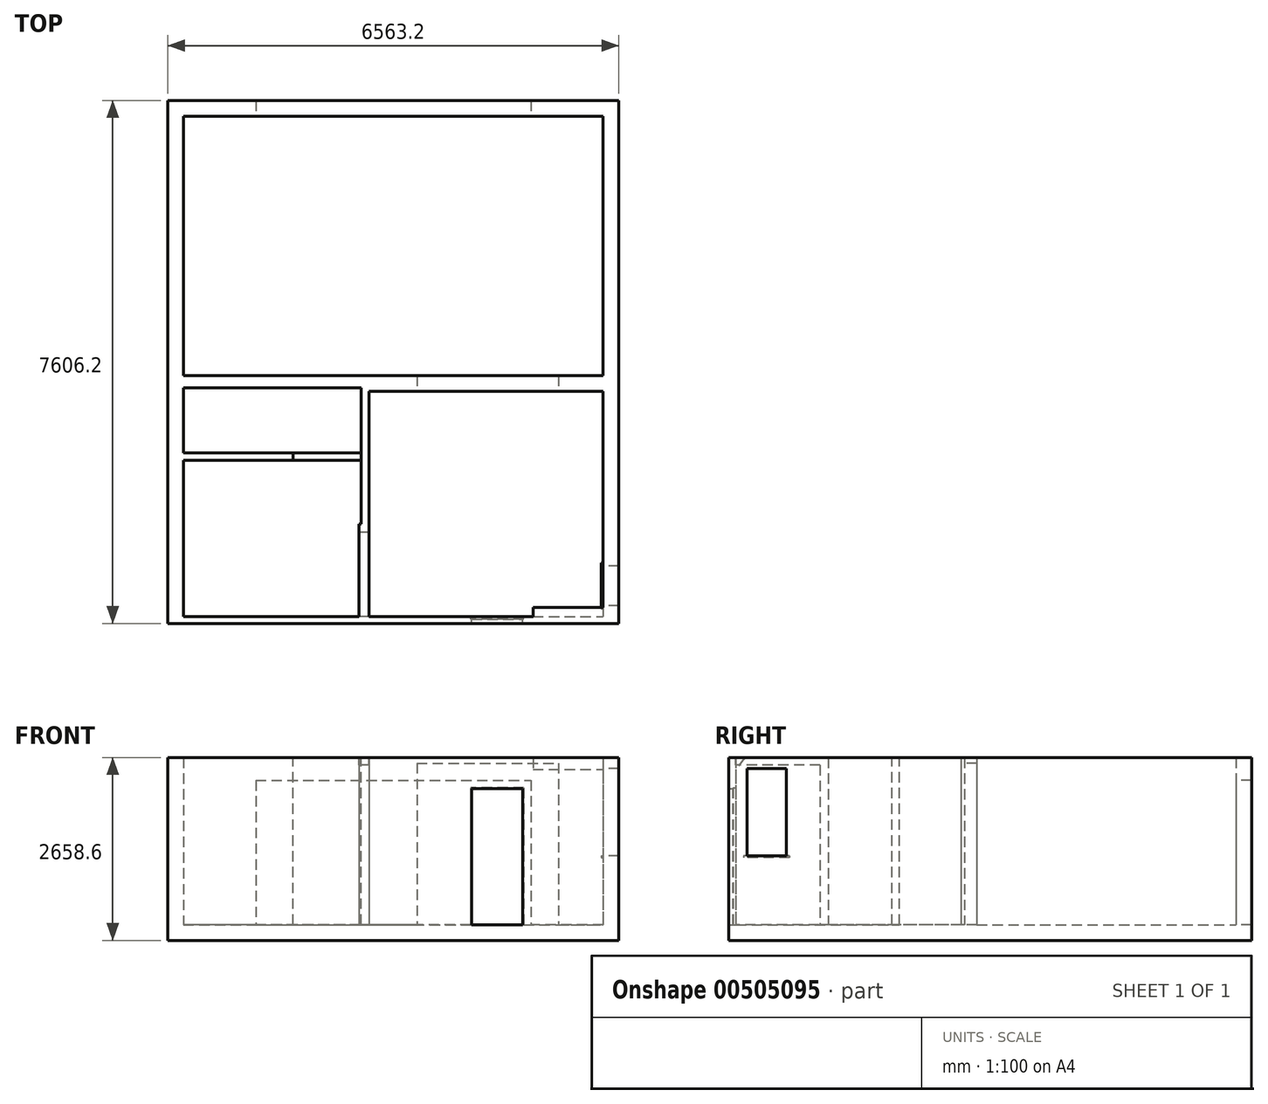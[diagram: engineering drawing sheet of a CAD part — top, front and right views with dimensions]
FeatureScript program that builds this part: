
annotation { "Feature Type Name" : "Feature", "Feature Type Description" : "" }
export const myFeature = defineFeature(function(context is Context, id is Id, definition is map)
    precondition{}
    {
        {
            var Q0;
            Q0=qCreatedBy(makeId("Top.planeOp"),FACE);
            var sketch = newSketch(context, id + "F0", { "sketchPlane" : qUnion([Q0])});
            skLineSegment(sketch, "E0", {"start": v(-3026.66, 951.57) * mm, "end": v(369.34, 951.57) * mm});
            skLineSegment(sketch, "E1", {"start": v(369.34, 951.57) * mm, "end": v(369.34, 722.97) * mm});
            skLineSegment(sketch, "E2", {"start": v(369.34, 722.97) * mm, "end": v(-327.66, 722.97) * mm});
            skLineSegment(sketch, "E3", {"start": v(-327.66, 722.97) * mm, "end": v(-327.66, -1327.03) * mm});
            skLineSegment(sketch, "E4", {"start": v(-327.66, -1327.03) * mm, "end": v(-1537.66, -1327.03) * mm});
            skLineSegment(sketch, "E5", {"start": v(-3255.26, 951.57) * mm, "end": v(-3255.26, -2250.1) * mm});
            skLineSegment(sketch, "E6", {"start": v(2429.34, 951.57) * mm, "end": v(3079.34, 951.57) * mm});
            skLineSegment(sketch, "E7", {"start": v(2429.34, 951.57) * mm, "end": v(2429.34, 722.97) * mm});
            skLineSegment(sketch, "E8", {"start": v(3307.94, 951.57) * mm, "end": v(3307.94, -2660.36) * mm});
            skLineSegment(sketch, "E9", {"start": v(2429.34, 722.97) * mm, "end": v(3079.34, 722.97) * mm});
            skLineSegment(sketch, "E10", {"start": v(3079.34, 722.97) * mm, "end": v(3079.34, -2553.03) * mm});
            skLineSegment(sketch, "E11", {"start": v(3079.34, 951.57) * mm, "end": v(3079.34, 4722.97) * mm});
            skLineSegment(sketch, "E12", {"start": v(3079.34, 4722.97) * mm, "end": v(-3026.66, 4722.97) * mm});
            skLineSegment(sketch, "E13", {"start": v(-3026.66, 4722.97) * mm, "end": v(-3026.66, 951.57) * mm});
            skLineSegment(sketch, "E14", {"start": v(-3255.26, 951.57) * mm, "end": v(-3255.26, 4951.57) * mm});
            skLineSegment(sketch, "E15", {"start": v(-3255.26, 4951.57) * mm, "end": v(3307.94, 4951.57) * mm});
            skLineSegment(sketch, "E16", {"start": v(3307.94, 4951.57) * mm, "end": v(3307.94, 951.57) * mm});
            skLineSegment(sketch, "E17", {"start": v(-1537.66, -2553.03) * mm, "end": v(3079.34, -2553.03) * mm});
            skLineSegment(sketch, "E18", {"start": v(-3255.26, -2654.63) * mm, "end": v(3307.94, -2654.63) * mm});
            skLineSegment(sketch, "E19", {"start": v(-1537.66, -2553.03) * mm, "end": v(-1537.66, -1327.03) * mm});
            skLineSegment(sketch, "E20", {"start": v(-1670.66, -1327.03) * mm, "end": v(-1670.66, -2553.03) * mm});
            skLineSegment(sketch, "E21", {"start": v(-1670.66, -2553.03) * mm, "end": v(-3026.66, -2553.03) * mm});
            skLineSegment(sketch, "E22", {"start": v(-3026.66, -2553.03) * mm, "end": v(-3026.66, -1327.03) * mm});
            skLineSegment(sketch, "E23", {"start": v(-3026.66, -1327.03) * mm, "end": v(-1670.66, -1327.03) * mm});
            skLineSegment(sketch, "E24", {"start": v(-3255.26, -2250.1) * mm, "end": v(-3255.26, -2654.63) * mm});
            skLineSegment(sketch, "E25", {"start": v(-2642.66, 772.97) * mm, "end": v(-1542.66, 772.97) * mm});
            skLineSegment(sketch, "E26", {"start": v(-442.66, 772.97) * mm, "end": v(-442.66, -1207.03) * mm});
            skLineSegment(sketch, "E27", {"start": v(-442.66, -1207.03) * mm, "end": v(-1432.66, -1207.03) * mm});
            skLineSegment(sketch, "E28", {"start": v(-1432.66, -1207.03) * mm, "end": v(-1432.66, 772.97) * mm});
            skLineSegment(sketch, "E29", {"start": v(-3026.66, -960.06) * mm, "end": v(-3026.66, -282.03) * mm});
            skLineSegment(sketch, "E30", {"start": v(-2642.66, 772.97) * mm, "end": v(-3026.66, 772.97) * mm});
            skLineSegment(sketch, "E31", {"start": v(-1542.66, 772.97) * mm, "end": v(-1542.66, -172.03) * mm});
            skLineSegment(sketch, "E32", {"start": v(-1542.66, -1212.03) * mm, "end": v(-3026.66, -1212.03) * mm});
            skLineSegment(sketch, "E33", {"start": v(-3026.66, -960.06) * mm, "end": v(-3026.66, -1212.03) * mm});
            skLineSegment(sketch, "E34", {"start": v(-3026.66, -172.03) * mm, "end": v(-3026.66, -172.03) * mm});
            skLineSegment(sketch, "E35", {"start": v(-3026.66, -282.03) * mm, "end": v(-1542.66, -282.03) * mm});
            skLineSegment(sketch, "E36", {"start": v(-3026.66, 0) * mm, "end": v(-3026.66, 772.97) * mm});
            skLineSegment(sketch, "E37", {"start": v(-3026.66, -172.03) * mm, "end": v(-1542.66, -172.03) * mm});
            skLineSegment(sketch, "E38", {"start": v(-3026.66, 0) * mm, "end": v(-3026.66, -172.03) * mm});
            skLineSegment(sketch, "E39.trimOffspring", {"start": v(-1542.66, -282.03) * mm, "end": v(-1542.66, -1212.03) * mm});
            skLineSegment(sketch, "E40.trimOffspring", {"start": v(-1432.66, 772.97) * mm, "end": v(-442.66, 772.97) * mm});
            skSolve(sketch);
        }
        {
            var Q0;
            Q0 = qSketchRegion(id + "F0", true);
            extrude(context, id + "F1", {"entities" : qUnion([Q0]), "depth" : 2430 * mm});
        }
        {
            var Q0;
            Q0=makeQuery(id+"F1.opExtrude","CAP_FACE",FACE,{"disambiguationData":[OSD([sQuery(id+"F0.wireOp",EDGE,"E0"),sQuery(id+"F0.wireOp",EDGE,"E1"),sQuery(id+"F0.wireOp",EDGE,"E2"),sQuery(id+"F0.wireOp",EDGE,"E3"),sQuery(id+"F0.wireOp",EDGE,"E4"),sQuery(id+"F0.wireOp",EDGE,"E5"),sQuery(id+"F0.wireOp",EDGE,"E6"),sQuery(id+"F0.wireOp",EDGE,"E7"),sQuery(id+"F0.wireOp",EDGE,"E8"),sQuery(id+"F0.wireOp",EDGE,"E9"),sQuery(id+"F0.wireOp",EDGE,"E10"),sQuery(id+"F0.wireOp",EDGE,"E11"),sQuery(id+"F0.wireOp",EDGE,"E12"),sQuery(id+"F0.wireOp",EDGE,"E13"),sQuery(id+"F0.wireOp",EDGE,"E14"),sQuery(id+"F0.wireOp",EDGE,"E15"),sQuery(id+"F0.wireOp",EDGE,"E16"),sQuery(id+"F0.wireOp",EDGE,"E17"),sQuery(id+"F0.wireOp",EDGE,"E18"),sQuery(id+"F0.wireOp",EDGE,"E19"),sQuery(id+"F0.wireOp",EDGE,"E20"),sQuery(id+"F0.wireOp",EDGE,"E21"),sQuery(id+"F0.wireOp",EDGE,"E22"),sQuery(id+"F0.wireOp",EDGE,"E23"),sQuery(id+"F0.wireOp",EDGE,"E24"),sQuery(id+"F0.wireOp",EDGE,"E25"),sQuery(id+"F0.wireOp",EDGE,"E26"),sQuery(id+"F0.wireOp",EDGE,"E27"),sQuery(id+"F0.wireOp",EDGE,"E28"),sQuery(id+"F0.wireOp",EDGE,"E29"),sQuery(id+"F0.wireOp",EDGE,"E30"),sQuery(id+"F0.wireOp",EDGE,"E31"),sQuery(id+"F0.wireOp",EDGE,"E32"),sQuery(id+"F0.wireOp",EDGE,"E33"),sQuery(id+"F0.wireOp",EDGE,"E35"),sQuery(id+"F0.wireOp",EDGE,"E36"),sQuery(id+"F0.wireOp",EDGE,"E37"),sQuery(id+"F0.wireOp",EDGE,"E38"),sQuery(id+"F0.wireOp",EDGE,"E39.trimOffspring"),sQuery(id+"F0.wireOp",EDGE,"E40.trimOffspring")])],"isStart":false});
            var sketch = newSketch(context, id + "F2", { "sketchPlane" : qUnion([Q0])});
            skLineSegment(sketch, "E41.bottom", {"start": v(-327.66, -1327.03) * mm, "end": v(-474.66, -1327.03) * mm});
            skLineSegment(sketch, "E41.top", {"start": v(-327.66, -2553.03) * mm, "end": v(-474.66, -2553.03) * mm});
            skLineSegment(sketch, "E41.left", {"start": v(-327.66, -1327.03) * mm, "end": v(-327.66, -2553.03) * mm});
            skLineSegment(sketch, "E41.right", {"start": v(-474.66, -1327.03) * mm, "end": v(-474.66, -2553.03) * mm});
            skSolve(sketch);
        }
        {
            var Q0;
            Q0 = qSketchRegion(id + "F2", true);
            extrude(context, id + "F3", {"entities" : qUnion([Q0]), "operationType" : NewBodyOperationType.ADD, "oppositeDirection" : true, "depth" : 110 * mm});
        }
        {
            var Q0;
            Q0=makeQuery(id+"F3.boolean.opBoolean","MERGE",FACE,{"derivedFrom":[makeQuery(id+"F1.opExtrude","CAP_FACE",FACE,{"disambiguationData":[OSD([sQuery(id+"F0.wireOp",EDGE,"E0"),sQuery(id+"F0.wireOp",EDGE,"E1"),sQuery(id+"F0.wireOp",EDGE,"E2"),sQuery(id+"F0.wireOp",EDGE,"E3"),sQuery(id+"F0.wireOp",EDGE,"E4"),sQuery(id+"F0.wireOp",EDGE,"E5"),sQuery(id+"F0.wireOp",EDGE,"E6"),sQuery(id+"F0.wireOp",EDGE,"E7"),sQuery(id+"F0.wireOp",EDGE,"E8"),sQuery(id+"F0.wireOp",EDGE,"E9"),sQuery(id+"F0.wireOp",EDGE,"E10"),sQuery(id+"F0.wireOp",EDGE,"E11"),sQuery(id+"F0.wireOp",EDGE,"E12"),sQuery(id+"F0.wireOp",EDGE,"E13"),sQuery(id+"F0.wireOp",EDGE,"E14"),sQuery(id+"F0.wireOp",EDGE,"E15"),sQuery(id+"F0.wireOp",EDGE,"E16"),sQuery(id+"F0.wireOp",EDGE,"E17"),sQuery(id+"F0.wireOp",EDGE,"E18"),sQuery(id+"F0.wireOp",EDGE,"E19"),sQuery(id+"F0.wireOp",EDGE,"E20"),sQuery(id+"F0.wireOp",EDGE,"E21"),sQuery(id+"F0.wireOp",EDGE,"E22"),sQuery(id+"F0.wireOp",EDGE,"E23"),sQuery(id+"F0.wireOp",EDGE,"E24"),sQuery(id+"F0.wireOp",EDGE,"E25"),sQuery(id+"F0.wireOp",EDGE,"E26"),sQuery(id+"F0.wireOp",EDGE,"E27"),sQuery(id+"F0.wireOp",EDGE,"E28"),sQuery(id+"F0.wireOp",EDGE,"E29"),sQuery(id+"F0.wireOp",EDGE,"E30"),sQuery(id+"F0.wireOp",EDGE,"E31"),sQuery(id+"F0.wireOp",EDGE,"E32"),sQuery(id+"F0.wireOp",EDGE,"E33"),sQuery(id+"F0.wireOp",EDGE,"E35"),sQuery(id+"F0.wireOp",EDGE,"E36"),sQuery(id+"F0.wireOp",EDGE,"E37"),sQuery(id+"F0.wireOp",EDGE,"E38"),sQuery(id+"F0.wireOp",EDGE,"E39.trimOffspring"),sQuery(id+"F0.wireOp",EDGE,"E40.trimOffspring")])],"isStart":false}),makeQuery(id+"F3.opExtrude","CAP_FACE",FACE,{"disambiguationData":[OSD([sQuery(id+"F2.wireOp",EDGE,"E41.bottom"),sQuery(id+"F2.wireOp",EDGE,"E41.top"),sQuery(id+"F2.wireOp",EDGE,"E41.left"),sQuery(id+"F2.wireOp",EDGE,"E41.right")])],"isStart":true})]});
            var sketch = newSketch(context, id + "F4", { "sketchPlane" : qUnion([Q0])});
            skLineSegment(sketch, "E42.bottom", {"start": v(369.34, 951.57) * mm, "end": v(2429.34, 951.57) * mm});
            skLineSegment(sketch, "E42.top", {"start": v(369.34, 722.97) * mm, "end": v(2429.34, 722.97) * mm});
            skLineSegment(sketch, "E42.left", {"start": v(369.34, 951.57) * mm, "end": v(369.34, 722.97) * mm});
            skLineSegment(sketch, "E42.right", {"start": v(2429.34, 951.57) * mm, "end": v(2429.34, 722.97) * mm});
            skSolve(sketch);
        }
        {
            var Q0;
            Q0 = qSketchRegion(id + "F4", true);
            extrude(context, id + "F5", {"entities" : qUnion([Q0]), "operationType" : NewBodyOperationType.ADD, "oppositeDirection" : true, "depth" : 80 * mm});
        }
        {
            var Q0;
            Q0=makeQuery(id+"F1.opExtrude","SWEPT_FACE",FACE,{"disambiguationData":[OSD([sQuery(id+"F0.wireOp",EDGE,"E10")])]});
            var sketch = newSketch(context, id + "F6", { "sketchPlane" : qUnion([Q0])});
            skLineSegment(sketch, "E43.bottom", {"start": v(1816.03, 2268) * mm, "end": v(2393.03, 2268) * mm});
            skLineSegment(sketch, "E43.top", {"start": v(1816.03, 998) * mm, "end": v(2393.03, 998) * mm});
            skLineSegment(sketch, "E43.left", {"start": v(1816.03, 2268) * mm, "end": v(1816.03, 998) * mm});
            skLineSegment(sketch, "E43.right", {"start": v(2393.03, 2268) * mm, "end": v(2393.03, 998) * mm});
            skSolve(sketch);
        }
        {
            var Q0;
            Q0 = qSketchRegion(id + "F6", true);
            extrude(context, id + "F7", {"entities" : qUnion([Q0]), "operationType" : NewBodyOperationType.REMOVE, "endBound" : BoundingType.UP_TO_NEXT, "oppositeDirection" : true, "depth" : 25.4 * mm});
        }
        {
            var Q0;
            Q0=makeQuery(id+"F1.opExtrude","SWEPT_FACE",FACE,{"disambiguationData":[OSD([sQuery(id+"F0.wireOp",EDGE,"E10")])]});
            var sketch = newSketch(context, id + "F8", { "sketchPlane" : qUnion([Q0])});
            skLineSegment(sketch, "E44.bottom", {"start": v(1771.03, 998) * mm, "end": v(2438.03, 998) * mm});
            skLineSegment(sketch, "E44.top", {"start": v(1771.03, 973) * mm, "end": v(2438.03, 973) * mm});
            skLineSegment(sketch, "E44.left", {"start": v(1771.03, 998) * mm, "end": v(1771.03, 973) * mm});
            skLineSegment(sketch, "E44.right", {"start": v(2438.03, 998) * mm, "end": v(2438.03, 973) * mm});
            skSolve(sketch);
        }
        {
            var Q0;
            Q0 = qSketchRegion(id + "F8", true);
            extrude(context, id + "F9", {"entities" : qUnion([Q0]), "operationType" : NewBodyOperationType.ADD, "depth" : 25 * mm});
        }
        {
            var Q0;
            Q0=makeQuery(id+"F1.opExtrude","SWEPT_FACE",FACE,{"disambiguationData":[OSD([sQuery(id+"F0.wireOp",EDGE,"E12")])]});
            var sketch = newSketch(context, id + "F10", { "sketchPlane" : qUnion([Q0])});
            skLineSegment(sketch, "E45.bottom", {"start": v(-1973.83, 2100) * mm, "end": v(2026.17, 2100) * mm});
            skLineSegment(sketch, "E45.top", {"start": v(-1973.83, 0) * mm, "end": v(2026.17, 0) * mm});
            skLineSegment(sketch, "E45.left", {"start": v(-1973.83, 2100) * mm, "end": v(-1973.83, 0) * mm});
            skLineSegment(sketch, "E45.right", {"start": v(2026.17, 2100) * mm, "end": v(2026.17, 0) * mm});
            skSolve(sketch);
        }
        {
            var Q0;
            Q0 = qSketchRegion(id + "F10", true);
            extrude(context, id + "F11", {"entities" : qUnion([Q0]), "operationType" : NewBodyOperationType.REMOVE, "endBound" : BoundingType.UP_TO_NEXT, "oppositeDirection" : true, "depth" : 25.4 * mm});
        }
        {
            var Q0;
            Q0=makeQuery(id+"F1.opExtrude","SWEPT_FACE",FACE,{"disambiguationData":[OSD([sQuery(id+"F0.wireOp",EDGE,"E17")])]});
            var sketch = newSketch(context, id + "F12", { "sketchPlane" : qUnion([Q0])});
            skLineSegment(sketch, "E46.bottom", {"start": v(-1909.34, 1978) * mm, "end": v(-1165.34, 1978) * mm});
            skLineSegment(sketch, "E46.top", {"start": v(-1909.34, 0) * mm, "end": v(-1165.34, 0) * mm});
            skLineSegment(sketch, "E46.left", {"start": v(-1909.34, 1978) * mm, "end": v(-1909.34, 0) * mm});
            skLineSegment(sketch, "E46.right", {"start": v(-1165.34, 1978) * mm, "end": v(-1165.34, 0) * mm});
            skSolve(sketch);
        }
        {
            var Q0;
            Q0 = qSketchRegion(id + "F12", true);
            extrude(context, id + "F13", {"entities" : qUnion([Q0]), "operationType" : NewBodyOperationType.REMOVE, "endBound" : BoundingType.UP_TO_NEXT, "oppositeDirection" : true, "depth" : 25.4 * mm});
        }
        {
            var Q0;
            Q0=makeQuery(id+"F1.opExtrude","SWEPT_FACE",FACE,{"disambiguationData":[OSD([sQuery(id+"F0.wireOp",EDGE,"E17")])]});
            var sketch = newSketch(context, id + "F14", { "sketchPlane" : qUnion([Q0])});
            skLineSegment(sketch, "E47.bottom", {"start": v(-1922.34, 1991) * mm, "end": v(-1152.34, 1991) * mm});
            skLineSegment(sketch, "E47.top", {"start": v(-1922.34, 0) * mm, "end": v(-1152.34, 0) * mm});
            skLineSegment(sketch, "E47.left", {"start": v(-1922.34, 1991) * mm, "end": v(-1922.34, 0) * mm});
            skLineSegment(sketch, "E47.right", {"start": v(-1152.34, 1991) * mm, "end": v(-1152.34, 0) * mm});
            skSolve(sketch);
        }
        {
            var Q0;
            Q0 = qSketchRegion(id + "F14", true);
            extrude(context, id + "F15", {"entities" : qUnion([Q0]), "operationType" : NewBodyOperationType.REMOVE, "oppositeDirection" : true, "depth" : 42 * mm});
        }
        {
            var Q0;
            {var subQ0=sQuery(id+"F0.wireOp",EDGE,"E26");var subQ1=sQuery(id+"F0.wireOp",EDGE,"E30");var subQ2=sQuery(id+"F0.wireOp",EDGE,"E25");var subQ3=sQuery(id+"F0.wireOp",EDGE,"E22");var subQ4=sQuery(id+"F0.wireOp",EDGE,"E21");var subQ5=sQuery(id+"F0.wireOp",EDGE,"E20");var subQ6=sQuery(id+"F0.wireOp",EDGE,"E19");var subQ7=sQuery(id+"F0.wireOp",EDGE,"E18");var subQ8=sQuery(id+"F0.wireOp",EDGE,"E17");var subQ9=sQuery(id+"F0.wireOp",EDGE,"E15");var subQ10=sQuery(id+"F0.wireOp",EDGE,"E28");var subQ11=sQuery(id+"F0.wireOp",EDGE,"E2");var subQ12=sQuery(id+"F0.wireOp",EDGE,"E13");var subQ13=sQuery(id+"F0.wireOp",EDGE,"E27");var subQ14=sQuery(id+"F0.wireOp",EDGE,"E1");var subQ15=sQuery(id+"F0.wireOp",EDGE,"E12");var subQ16=sQuery(id+"F0.wireOp",EDGE,"E3");var subQ17=sQuery(id+"F0.wireOp",EDGE,"E23");var subQ18=sQuery(id+"F0.wireOp",EDGE,"E0");var subQ19=sQuery(id+"F0.wireOp",EDGE,"E9");var subQ20=sQuery(id+"F0.wireOp",EDGE,"E4");var subQ21=sQuery(id+"F0.wireOp",EDGE,"E24");var subQ22=sQuery(id+"F0.wireOp",EDGE,"E14");var subQ23=sQuery(id+"F0.wireOp",EDGE,"E5");var subQ24=sQuery(id+"F0.wireOp",EDGE,"E6");var subQ25=sQuery(id+"F0.wireOp",EDGE,"E33");var subQ26=sQuery(id+"F0.wireOp",EDGE,"E29");var subQ27=sQuery(id+"F0.wireOp",EDGE,"E31");var subQ28=sQuery(id+"F0.wireOp",EDGE,"E32");var subQ29=sQuery(id+"F0.wireOp",EDGE,"E35");var subQ30=sQuery(id+"F0.wireOp",EDGE,"E38");var subQ31=sQuery(id+"F0.wireOp",EDGE,"E36");var subQ32=sQuery(id+"F0.wireOp",EDGE,"E37");var subQ33=sQuery(id+"F0.wireOp",EDGE,"E39.trimOffspring");var subQ34=sQuery(id+"F0.wireOp",EDGE,"E40.trimOffspring");Q0=makeQuery(id+"F13.boolean.opBoolean","SPLIT",FACE,{"disambiguationData":[TD([makeQuery(id+"F1.opExtrude","SWEPT_FACE",FACE,{"disambiguationData":[OSD([subQ14])]})])],"derivedFrom":makeQuery(id+"F1.opExtrude","CAP_FACE",FACE,{"disambiguationData":[OSD([subQ18,subQ14,subQ11,subQ16,subQ20,subQ23,subQ24,sQuery(id+"F0.wireOp",EDGE,"E7"),sQuery(id+"F0.wireOp",EDGE,"E8"),subQ19,sQuery(id+"F0.wireOp",EDGE,"E10"),sQuery(id+"F0.wireOp",EDGE,"E11"),subQ15,subQ12,subQ22,subQ9,sQuery(id+"F0.wireOp",EDGE,"E16"),subQ8,subQ7,subQ6,subQ5,subQ4,subQ3,subQ17,subQ21,subQ2,subQ0,subQ13,subQ10,subQ26,subQ1,subQ27,subQ28,subQ25,subQ29,subQ31,subQ32,subQ30,subQ33,subQ34])],"isStart":true})});}
            var sketch = newSketch(context, id + "F16", { "sketchPlane" : qUnion([Q0])});
            skLineSegment(sketch, "E48.bottom", {"start": v(-3255.26, -4951.57) * mm, "end": v(3307.94, -4951.57) * mm});
            skLineSegment(sketch, "E48.top", {"start": v(-3255.26, 2654.63) * mm, "end": v(3307.94, 2654.63) * mm});
            skLineSegment(sketch, "E48.left", {"start": v(-3255.26, -4951.57) * mm, "end": v(-3255.26, 2654.63) * mm});
            skLineSegment(sketch, "E48.right", {"start": v(3307.94, -4951.57) * mm, "end": v(3307.94, 2654.63) * mm});
            skSolve(sketch);
        }
        {
            var Q0;
            Q0 = qSketchRegion(id + "F16", true);
            extrude(context, id + "F17", {"entities" : qUnion([Q0]), "operationType" : NewBodyOperationType.ADD, "depth" : 228.6 * mm});
        }
        {
            var Q0;
            Q0=makeQuery(id+"F1.opExtrude","SWEPT_FACE",FACE,{"disambiguationData":[OSD([sQuery(id+"F0.wireOp",EDGE,"E10")])]});
            var sketch = newSketch(context, id + "F18", { "sketchPlane" : qUnion([Q0])});
            skLineSegment(sketch, "E49", {"start": v(2553.03, 2430) * mm, "end": v(2423.03, 2430) * mm});
            skLineSegment(sketch, "E50", {"start": v(2423.03, 2430) * mm, "end": v(2553.03, 2260) * mm});
            skLineSegment(sketch, "E51", {"start": v(2553.03, 2260) * mm, "end": v(2553.03, 2430) * mm});
            skSolve(sketch);
        }
        {
            var Q0;
            Q0 = qSketchRegion(id + "F18", true);
            extrude(context, id + "F19", {"entities" : qUnion([Q0]), "operationType" : NewBodyOperationType.ADD, "depth" : 1020 * mm});
        }
        {
            var Q0;
            Q0=makeQuery(id+"F19.boolean.opBoolean","MERGE",FACE,{"derivedFrom":[makeQuery(id+"F5.boolean.opBoolean","MERGE",FACE,{"derivedFrom":[makeQuery(id+"F3.boolean.opBoolean","MERGE",FACE,{"derivedFrom":[makeQuery(id+"F1.opExtrude","CAP_FACE",FACE,{"disambiguationData":[OSD([sQuery(id+"F0.wireOp",EDGE,"E0"),sQuery(id+"F0.wireOp",EDGE,"E1"),sQuery(id+"F0.wireOp",EDGE,"E2"),sQuery(id+"F0.wireOp",EDGE,"E3"),sQuery(id+"F0.wireOp",EDGE,"E4"),sQuery(id+"F0.wireOp",EDGE,"E5"),sQuery(id+"F0.wireOp",EDGE,"E6"),sQuery(id+"F0.wireOp",EDGE,"E7"),sQuery(id+"F0.wireOp",EDGE,"E8"),sQuery(id+"F0.wireOp",EDGE,"E9"),sQuery(id+"F0.wireOp",EDGE,"E10"),sQuery(id+"F0.wireOp",EDGE,"E11"),sQuery(id+"F0.wireOp",EDGE,"E12"),sQuery(id+"F0.wireOp",EDGE,"E13"),sQuery(id+"F0.wireOp",EDGE,"E14"),sQuery(id+"F0.wireOp",EDGE,"E15"),sQuery(id+"F0.wireOp",EDGE,"E16"),sQuery(id+"F0.wireOp",EDGE,"E17"),sQuery(id+"F0.wireOp",EDGE,"E18"),sQuery(id+"F0.wireOp",EDGE,"E19"),sQuery(id+"F0.wireOp",EDGE,"E20"),sQuery(id+"F0.wireOp",EDGE,"E21"),sQuery(id+"F0.wireOp",EDGE,"E22"),sQuery(id+"F0.wireOp",EDGE,"E23"),sQuery(id+"F0.wireOp",EDGE,"E24"),sQuery(id+"F0.wireOp",EDGE,"E25"),sQuery(id+"F0.wireOp",EDGE,"E26"),sQuery(id+"F0.wireOp",EDGE,"E27"),sQuery(id+"F0.wireOp",EDGE,"E28"),sQuery(id+"F0.wireOp",EDGE,"E29"),sQuery(id+"F0.wireOp",EDGE,"E30"),sQuery(id+"F0.wireOp",EDGE,"E31"),sQuery(id+"F0.wireOp",EDGE,"E32"),sQuery(id+"F0.wireOp",EDGE,"E33"),sQuery(id+"F0.wireOp",EDGE,"E35"),sQuery(id+"F0.wireOp",EDGE,"E36"),sQuery(id+"F0.wireOp",EDGE,"E37"),sQuery(id+"F0.wireOp",EDGE,"E38"),sQuery(id+"F0.wireOp",EDGE,"E39.trimOffspring"),sQuery(id+"F0.wireOp",EDGE,"E40.trimOffspring")])],"isStart":false}),makeQuery(id+"F3.opExtrude","CAP_FACE",FACE,{"disambiguationData":[OSD([sQuery(id+"F2.wireOp",EDGE,"E41.bottom"),sQuery(id+"F2.wireOp",EDGE,"E41.top"),sQuery(id+"F2.wireOp",EDGE,"E41.left"),sQuery(id+"F2.wireOp",EDGE,"E41.right")])],"isStart":true})]}),makeQuery(id+"F5.opExtrude","CAP_FACE",FACE,{"disambiguationData":[OSD([sQuery(id+"F4.wireOp",EDGE,"E42.bottom"),sQuery(id+"F4.wireOp",EDGE,"E42.top"),sQuery(id+"F4.wireOp",EDGE,"E42.left"),sQuery(id+"F4.wireOp",EDGE,"E42.right")])],"isStart":true})]}),makeQuery(id+"F19.opExtrude","SWEPT_FACE",FACE,{"disambiguationData":[OSD([sQuery(id+"F18.wireOp",EDGE,"E49")])]})]});
            var sketch = newSketch(context, id + "F20", { "sketchPlane" : qUnion([Q0])});
            skLineSegment(sketch, "E52.bottom", {"start": v(-3026.66, -282.03) * mm, "end": v(-474.66, -282.03) * mm});
            skLineSegment(sketch, "E52.top", {"start": v(-3026.66, -2553.03) * mm, "end": v(-474.66, -2553.03) * mm});
            skLineSegment(sketch, "E52.left", {"start": v(-3026.66, -282.03) * mm, "end": v(-3026.66, -2553.03) * mm});
            skLineSegment(sketch, "E52.right", {"start": v(-474.66, -282.03) * mm, "end": v(-474.66, -2553.03) * mm});
            skSolve(sketch);
        }
        {
            var Q0;
            Q0 = qSketchRegion(id + "F20", true);
            var Q1;
            {var subQ2=sQuery(id+"F16.wireOp",EDGE,"E48.bottom");var subQ3=sQuery(id+"F16.wireOp",EDGE,"E48.top");Q1=makeQuery(id+"F17.boolean.opBoolean","SPLIT",FACE,{"disambiguationData":[TD([makeQuery(id+"F1.opExtrude","SWEPT_FACE",FACE,{"disambiguationData":[OSD([sQuery(id+"F0.wireOp",EDGE,"E0")])]})])],"derivedFrom":makeQuery(id+"F17.opExtrude","CAP_FACE",FACE,{"disambiguationData":[OSD([subQ2,subQ3,sQuery(id+"F16.wireOp",EDGE,"E48.left"),sQuery(id+"F16.wireOp",EDGE,"E48.right")])],"isStart":true})});}
            extrude(context, id + "F21", {"entities" : qUnion([Q0]), "operationType" : NewBodyOperationType.REMOVE, "endBound" : BoundingType.UP_TO_SURFACE, "oppositeDirection" : true, "depth" : 25 * mm, "endBoundEntityFace" : qUnion([Q1]), "offsetDistance" : 25 * mm});
        }
        {
            var Q0;
            Q0=makeQuery(id+"F19.boolean.opBoolean","MERGE",FACE,{"derivedFrom":[makeQuery(id+"F5.boolean.opBoolean","MERGE",FACE,{"derivedFrom":[makeQuery(id+"F3.boolean.opBoolean","MERGE",FACE,{"derivedFrom":[makeQuery(id+"F1.opExtrude","CAP_FACE",FACE,{"disambiguationData":[OSD([sQuery(id+"F0.wireOp",EDGE,"E0"),sQuery(id+"F0.wireOp",EDGE,"E1"),sQuery(id+"F0.wireOp",EDGE,"E2"),sQuery(id+"F0.wireOp",EDGE,"E3"),sQuery(id+"F0.wireOp",EDGE,"E4"),sQuery(id+"F0.wireOp",EDGE,"E5"),sQuery(id+"F0.wireOp",EDGE,"E6"),sQuery(id+"F0.wireOp",EDGE,"E7"),sQuery(id+"F0.wireOp",EDGE,"E8"),sQuery(id+"F0.wireOp",EDGE,"E9"),sQuery(id+"F0.wireOp",EDGE,"E10"),sQuery(id+"F0.wireOp",EDGE,"E11"),sQuery(id+"F0.wireOp",EDGE,"E12"),sQuery(id+"F0.wireOp",EDGE,"E13"),sQuery(id+"F0.wireOp",EDGE,"E14"),sQuery(id+"F0.wireOp",EDGE,"E15"),sQuery(id+"F0.wireOp",EDGE,"E16"),sQuery(id+"F0.wireOp",EDGE,"E17"),sQuery(id+"F0.wireOp",EDGE,"E18"),sQuery(id+"F0.wireOp",EDGE,"E19"),sQuery(id+"F0.wireOp",EDGE,"E20"),sQuery(id+"F0.wireOp",EDGE,"E21"),sQuery(id+"F0.wireOp",EDGE,"E22"),sQuery(id+"F0.wireOp",EDGE,"E23"),sQuery(id+"F0.wireOp",EDGE,"E24"),sQuery(id+"F0.wireOp",EDGE,"E25"),sQuery(id+"F0.wireOp",EDGE,"E26"),sQuery(id+"F0.wireOp",EDGE,"E27"),sQuery(id+"F0.wireOp",EDGE,"E28"),sQuery(id+"F0.wireOp",EDGE,"E29"),sQuery(id+"F0.wireOp",EDGE,"E30"),sQuery(id+"F0.wireOp",EDGE,"E31"),sQuery(id+"F0.wireOp",EDGE,"E32"),sQuery(id+"F0.wireOp",EDGE,"E33"),sQuery(id+"F0.wireOp",EDGE,"E35"),sQuery(id+"F0.wireOp",EDGE,"E36"),sQuery(id+"F0.wireOp",EDGE,"E37"),sQuery(id+"F0.wireOp",EDGE,"E38"),sQuery(id+"F0.wireOp",EDGE,"E39.trimOffspring"),sQuery(id+"F0.wireOp",EDGE,"E40.trimOffspring")])],"isStart":false}),makeQuery(id+"F3.opExtrude","CAP_FACE",FACE,{"disambiguationData":[OSD([sQuery(id+"F2.wireOp",EDGE,"E41.bottom"),sQuery(id+"F2.wireOp",EDGE,"E41.top"),sQuery(id+"F2.wireOp",EDGE,"E41.left"),sQuery(id+"F2.wireOp",EDGE,"E41.right")])],"isStart":true})]}),makeQuery(id+"F5.opExtrude","CAP_FACE",FACE,{"disambiguationData":[OSD([sQuery(id+"F4.wireOp",EDGE,"E42.bottom"),sQuery(id+"F4.wireOp",EDGE,"E42.top"),sQuery(id+"F4.wireOp",EDGE,"E42.left"),sQuery(id+"F4.wireOp",EDGE,"E42.right")])],"isStart":true})]}),makeQuery(id+"F19.opExtrude","SWEPT_FACE",FACE,{"disambiguationData":[OSD([sQuery(id+"F18.wireOp",EDGE,"E49")])]})]});
            var sketch = newSketch(context, id + "F22", { "sketchPlane" : qUnion([Q0])});
            skLineSegment(sketch, "E53.bottom", {"start": v(-1432.66, -282.03) * mm, "end": v(-442.66, -282.03) * mm});
            skLineSegment(sketch, "E53.top", {"start": v(-1432.66, -172.03) * mm, "end": v(-442.66, -172.03) * mm});
            skLineSegment(sketch, "E53.left", {"start": v(-1432.66, -282.03) * mm, "end": v(-1432.66, -172.03) * mm});
            skLineSegment(sketch, "E53.right", {"start": v(-442.66, -282.03) * mm, "end": v(-442.66, -172.03) * mm});
            skSolve(sketch);
        }
        {
            var Q0;
            Q0 = qSketchRegion(id + "F22", true);
            var Q1;
            {var subQ0=sQuery(id+"F16.wireOp",EDGE,"E48.top");var subQ1=sQuery(id+"F16.wireOp",EDGE,"E48.bottom");var subQ2=makeQuery(id+"F17.opExtrude","CAP_FACE",FACE,{"disambiguationData":[OSD([subQ1,subQ0,sQuery(id+"F16.wireOp",EDGE,"E48.left"),sQuery(id+"F16.wireOp",EDGE,"E48.right")])],"isStart":true});Q1=makeQuery(id+"F21.boolean.opBoolean","MERGE",FACE,{"derivedFrom":[makeQuery(id+"F17.boolean.opBoolean","SPLIT",FACE,{"disambiguationData":[TD([makeQuery(id+"F1.opExtrude","SWEPT_FACE",FACE,{"disambiguationData":[OSD([sQuery(id+"F0.wireOp",EDGE,"E0")])]})])],"derivedFrom":subQ2}),makeQuery(id+"F17.boolean.opBoolean","SPLIT",FACE,{"disambiguationData":[TD([makeQuery(id+"F1.opExtrude","SWEPT_FACE",FACE,{"disambiguationData":[OSD([sQuery(id+"F0.wireOp",EDGE,"E20")])]})])],"derivedFrom":subQ2}),makeQuery(id+"F17.boolean.opBoolean","SPLIT",FACE,{"disambiguationData":[TD([makeQuery(id+"F1.opExtrude","SWEPT_FACE",FACE,{"disambiguationData":[OSD([sQuery(id+"F0.wireOp",EDGE,"E26")])]})])],"derivedFrom":subQ2}),makeQuery(id+"F17.boolean.opBoolean","SPLIT",FACE,{"disambiguationData":[TD([makeQuery(id+"F1.opExtrude","SWEPT_FACE",FACE,{"disambiguationData":[OSD([sQuery(id+"F0.wireOp",EDGE,"E32")])]})])],"derivedFrom":subQ2}),makeQuery(id+"F21.opExtrude","CAP_FACE",FACE,{"disambiguationData":[OSD([sQuery(id+"F20.wireOp",EDGE,"E52.bottom"),sQuery(id+"F20.wireOp",EDGE,"E52.top"),sQuery(id+"F20.wireOp",EDGE,"E52.left"),sQuery(id+"F20.wireOp",EDGE,"E52.right")])],"isStart":false})]});}
            extrude(context, id + "F23", {"entities" : qUnion([Q0]), "endBound" : BoundingType.UP_TO_SURFACE, "oppositeDirection" : true, "depth" : 25 * mm, "endBoundEntityFace" : qUnion([Q1]), "offsetDistance" : 25 * mm});
        }
        {
            var Q0;
            Q0=makeQuery(id+"F19.boolean.opBoolean","MERGE",FACE,{"derivedFrom":[makeQuery(id+"F5.boolean.opBoolean","MERGE",FACE,{"derivedFrom":[makeQuery(id+"F3.boolean.opBoolean","MERGE",FACE,{"derivedFrom":[makeQuery(id+"F1.opExtrude","CAP_FACE",FACE,{"disambiguationData":[OSD([sQuery(id+"F0.wireOp",EDGE,"E0"),sQuery(id+"F0.wireOp",EDGE,"E1"),sQuery(id+"F0.wireOp",EDGE,"E2"),sQuery(id+"F0.wireOp",EDGE,"E3"),sQuery(id+"F0.wireOp",EDGE,"E4"),sQuery(id+"F0.wireOp",EDGE,"E5"),sQuery(id+"F0.wireOp",EDGE,"E6"),sQuery(id+"F0.wireOp",EDGE,"E7"),sQuery(id+"F0.wireOp",EDGE,"E8"),sQuery(id+"F0.wireOp",EDGE,"E9"),sQuery(id+"F0.wireOp",EDGE,"E10"),sQuery(id+"F0.wireOp",EDGE,"E11"),sQuery(id+"F0.wireOp",EDGE,"E12"),sQuery(id+"F0.wireOp",EDGE,"E13"),sQuery(id+"F0.wireOp",EDGE,"E14"),sQuery(id+"F0.wireOp",EDGE,"E15"),sQuery(id+"F0.wireOp",EDGE,"E16"),sQuery(id+"F0.wireOp",EDGE,"E17"),sQuery(id+"F0.wireOp",EDGE,"E18"),sQuery(id+"F0.wireOp",EDGE,"E19"),sQuery(id+"F0.wireOp",EDGE,"E20"),sQuery(id+"F0.wireOp",EDGE,"E21"),sQuery(id+"F0.wireOp",EDGE,"E22"),sQuery(id+"F0.wireOp",EDGE,"E23"),sQuery(id+"F0.wireOp",EDGE,"E24"),sQuery(id+"F0.wireOp",EDGE,"E25"),sQuery(id+"F0.wireOp",EDGE,"E26"),sQuery(id+"F0.wireOp",EDGE,"E27"),sQuery(id+"F0.wireOp",EDGE,"E28"),sQuery(id+"F0.wireOp",EDGE,"E29"),sQuery(id+"F0.wireOp",EDGE,"E30"),sQuery(id+"F0.wireOp",EDGE,"E31"),sQuery(id+"F0.wireOp",EDGE,"E32"),sQuery(id+"F0.wireOp",EDGE,"E33"),sQuery(id+"F0.wireOp",EDGE,"E35"),sQuery(id+"F0.wireOp",EDGE,"E36"),sQuery(id+"F0.wireOp",EDGE,"E37"),sQuery(id+"F0.wireOp",EDGE,"E38"),sQuery(id+"F0.wireOp",EDGE,"E39.trimOffspring"),sQuery(id+"F0.wireOp",EDGE,"E40.trimOffspring")])],"isStart":false}),makeQuery(id+"F3.opExtrude","CAP_FACE",FACE,{"disambiguationData":[OSD([sQuery(id+"F2.wireOp",EDGE,"E41.bottom"),sQuery(id+"F2.wireOp",EDGE,"E41.top"),sQuery(id+"F2.wireOp",EDGE,"E41.left"),sQuery(id+"F2.wireOp",EDGE,"E41.right")])],"isStart":true})]}),makeQuery(id+"F5.opExtrude","CAP_FACE",FACE,{"disambiguationData":[OSD([sQuery(id+"F4.wireOp",EDGE,"E42.bottom"),sQuery(id+"F4.wireOp",EDGE,"E42.top"),sQuery(id+"F4.wireOp",EDGE,"E42.left"),sQuery(id+"F4.wireOp",EDGE,"E42.right")])],"isStart":true})]}),makeQuery(id+"F19.opExtrude","SWEPT_FACE",FACE,{"disambiguationData":[OSD([sQuery(id+"F18.wireOp",EDGE,"E49")])]})]});
            var sketch = newSketch(context, id + "F24", { "sketchPlane" : qUnion([Q0])});
            skLineSegment(sketch, "E54.bottom", {"start": v(-1542.66, 772.97) * mm, "end": v(-1432.66, 772.97) * mm});
            skLineSegment(sketch, "E54.top", {"start": v(-1542.66, -172.03) * mm, "end": v(-1432.66, -172.03) * mm});
            skLineSegment(sketch, "E54.left", {"start": v(-1542.66, 772.97) * mm, "end": v(-1542.66, -172.03) * mm});
            skLineSegment(sketch, "E54.right", {"start": v(-1432.66, 772.97) * mm, "end": v(-1432.66, -172.03) * mm});
            skSolve(sketch);
        }
        {
            var Q0;
            Q0 = qSketchRegion(id + "F24", true);
            var Q1;
            {var subQ0=sQuery(id+"F16.wireOp",EDGE,"E48.top");var subQ1=sQuery(id+"F16.wireOp",EDGE,"E48.bottom");var subQ2=makeQuery(id+"F17.opExtrude","CAP_FACE",FACE,{"disambiguationData":[OSD([subQ1,subQ0,sQuery(id+"F16.wireOp",EDGE,"E48.left"),sQuery(id+"F16.wireOp",EDGE,"E48.right")])],"isStart":true});Q1=makeQuery(id+"F21.boolean.opBoolean","MERGE",FACE,{"derivedFrom":[makeQuery(id+"F17.boolean.opBoolean","SPLIT",FACE,{"disambiguationData":[TD([makeQuery(id+"F1.opExtrude","SWEPT_FACE",FACE,{"disambiguationData":[OSD([sQuery(id+"F0.wireOp",EDGE,"E0")])]})])],"derivedFrom":subQ2}),makeQuery(id+"F17.boolean.opBoolean","SPLIT",FACE,{"disambiguationData":[TD([makeQuery(id+"F1.opExtrude","SWEPT_FACE",FACE,{"disambiguationData":[OSD([sQuery(id+"F0.wireOp",EDGE,"E20")])]})])],"derivedFrom":subQ2}),makeQuery(id+"F17.boolean.opBoolean","SPLIT",FACE,{"disambiguationData":[TD([makeQuery(id+"F1.opExtrude","SWEPT_FACE",FACE,{"disambiguationData":[OSD([sQuery(id+"F0.wireOp",EDGE,"E26")])]})])],"derivedFrom":subQ2}),makeQuery(id+"F17.boolean.opBoolean","SPLIT",FACE,{"disambiguationData":[TD([makeQuery(id+"F1.opExtrude","SWEPT_FACE",FACE,{"disambiguationData":[OSD([sQuery(id+"F0.wireOp",EDGE,"E32")])]})])],"derivedFrom":subQ2}),makeQuery(id+"F21.opExtrude","CAP_FACE",FACE,{"disambiguationData":[OSD([sQuery(id+"F20.wireOp",EDGE,"E52.bottom"),sQuery(id+"F20.wireOp",EDGE,"E52.top"),sQuery(id+"F20.wireOp",EDGE,"E52.left"),sQuery(id+"F20.wireOp",EDGE,"E52.right")])],"isStart":false})]});}
            extrude(context, id + "F25", {"entities" : qUnion([Q0]), "operationType" : NewBodyOperationType.REMOVE, "endBound" : BoundingType.UP_TO_SURFACE, "oppositeDirection" : true, "depth" : 25 * mm, "endBoundEntityFace" : qUnion([Q1]), "offsetDistance" : 25 * mm});
        }
    });
